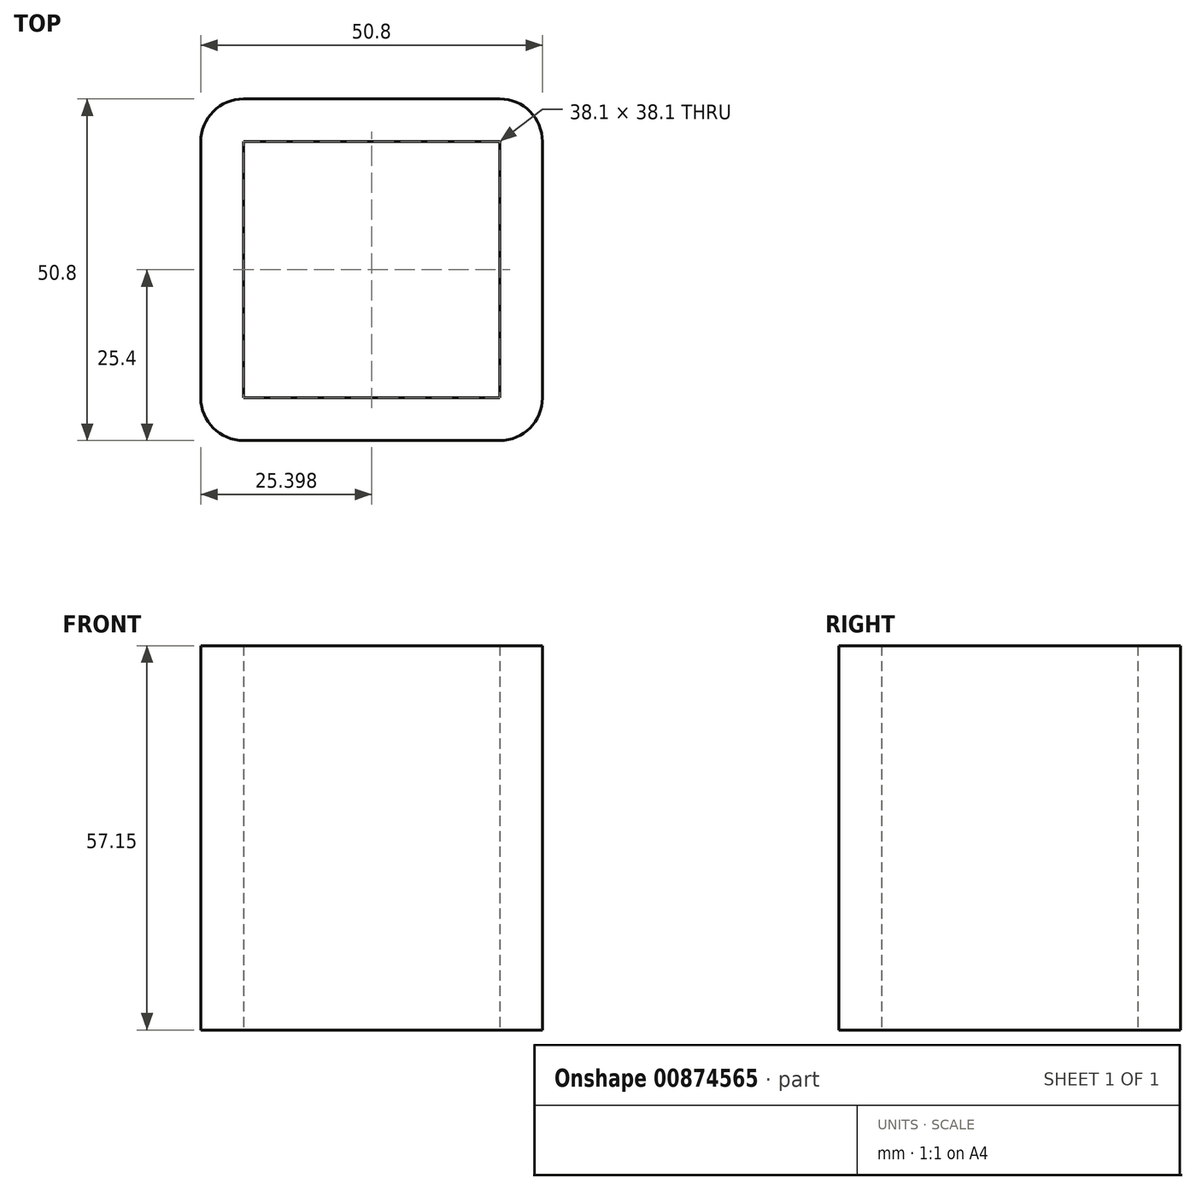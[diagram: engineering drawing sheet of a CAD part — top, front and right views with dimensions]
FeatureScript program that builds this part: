
annotation { "Feature Type Name" : "Feature", "Feature Type Description" : "" }
export const myFeature = defineFeature(function(context is Context, id is Id, definition is map)
    precondition{}
    {
        {
            var Q0;
            Q0=qCreatedBy(makeId("Top.planeOp"),FACE);
            var sketch = newSketch(context, id + "F0", { "sketchPlane" : qUnion([Q0])});
            skLineSegment(sketch, "E0.bottom", {"start": v(-21.67, -25.4) * mm, "end": v(16.43, -25.4) * mm});
            skLineSegment(sketch, "E0.top", {"start": v(-21.67, 25.4) * mm, "end": v(16.43, 25.4) * mm});
            skLineSegment(sketch, "E0.left", {"start": v(-28.02, -19.05) * mm, "end": v(-28.02, 19.05) * mm});
            skLineSegment(sketch, "E0.right", {"start": v(22.78, -19.05) * mm, "end": v(22.78, 19.05) * mm});
            skPoint(sketch, "E0.middle", {"position": v(-2.62, 0) * mm});
            skPoint(sketch, "E1.visualSharp", {"position": v(-28.02, -25.4) * mm});
            skArc(sketch, "E1.filletArc", {"start": v(-28.02, -19.05) * mm, "mid": v(-26.16, -23.54) * mm, "end": v(-21.67, -25.4) * mm});
            skPoint(sketch, "E2.visualSharp", {"position": v(22.78, -25.4) * mm});
            skArc(sketch, "E2.filletArc", {"start": v(16.43, -25.4) * mm, "mid": v(20.92, -23.54) * mm, "end": v(22.78, -19.05) * mm});
            skPoint(sketch, "E3.visualSharp", {"position": v(22.78, 25.4) * mm});
            skArc(sketch, "E3.filletArc", {"start": v(22.78, 19.05) * mm, "mid": v(20.92, 23.54) * mm, "end": v(16.43, 25.4) * mm});
            skPoint(sketch, "E4.visualSharp", {"position": v(-28.02, 25.4) * mm});
            skArc(sketch, "E4.filletArc", {"start": v(-21.67, 25.4) * mm, "mid": v(-26.16, 23.54) * mm, "end": v(-28.02, 19.05) * mm});
            skLineSegment(sketch, "E5.0", {"start": v(-21.67, -19.05) * mm, "end": v(16.43, -19.05) * mm});
            skLineSegment(sketch, "E5.1", {"start": v(-21.67, -19.05) * mm, "end": v(-21.67, 19.05) * mm});
            skLineSegment(sketch, "E5.2", {"start": v(-21.67, 19.05) * mm, "end": v(16.43, 19.05) * mm});
            skLineSegment(sketch, "E5.3", {"start": v(16.43, -19.05) * mm, "end": v(16.43, 19.05) * mm});
            skSolve(sketch);
        }
        {
            var Q0;
            Q0=makeQuery(id+"F0.imprint","IMPRINT",FACE,{"disambiguationData":[TD([[makeQuery(id+"F0.imprint","IMPRINT",EDGE,{"derivedFrom":sQuery(id+"F0.wireOp",EDGE,"E0.bottom")}),1.0]])]});
            extrude(context, id + "F1", {"entities" : qUnion([Q0]), "depth" : 57.15 * mm, "offsetDistance" : 25.4 * mm});
        }
    });
